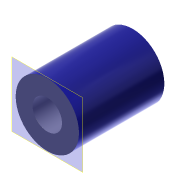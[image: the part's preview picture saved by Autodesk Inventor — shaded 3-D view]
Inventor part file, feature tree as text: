
AUTODESK INVENTOR PART (.ipt)
format: ipt  version: 2018.1 (Build 221171000, 171)  size: 157,696 bytes
history: native  units: mm
features: other x6, sketch x3, extrude x1, sweep x1
ambient origin geometry x8: Origin, YZ Plane, XZ Plane, XY Plane, X Axis, Y Axis, Z Axis, Center Point
bodies: Body1 (feature_tree)
feature tree (11):
  other  "Твердое тело1"
  other  "РабПлоскость1"
  sketch  "Эскиз1"
  other  "РабПлоскость2"
  extrude  "Выдавливание1"  Depth=21.5mm
  sweep  "Сдвиг1"
  sketch  "Эскиз2"
  sketch  "3D эскиз1"
  parser-record x1  (decoder bookkeeping rows leaked as tree rows — omitted from the tree; the rows remain in map.json)
  other  "0837 solenoid.iam"
  other  "frame:1"
note: 1 file-system path scrubbed to <path> (originals preserved in map.json)
